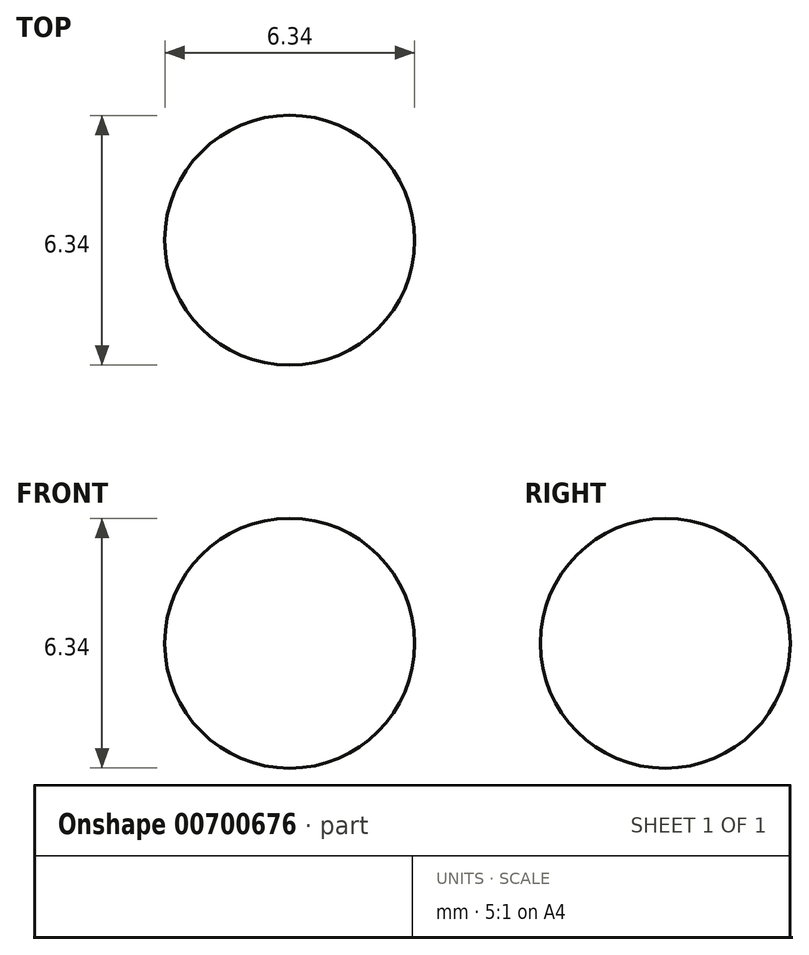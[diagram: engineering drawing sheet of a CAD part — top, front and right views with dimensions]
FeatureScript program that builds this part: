
annotation { "Feature Type Name" : "Feature", "Feature Type Description" : "" }
export const myFeature = defineFeature(function(context is Context, id is Id, definition is map)
    precondition{}
    {
        {
            var Q0;
            Q0=qCreatedBy(makeId("Front.planeOp"),FACE);
            var sketch = newSketch(context, id + "F0", { "sketchPlane" : qUnion([Q0])});
            skArc(sketch, "E0", {"start": v(0, -3.18) * mm, "mid": v(3.18, 0) * mm, "end": v(0, 3.18) * mm});
            skLineSegment(sketch, "E1", {"start": v(0, 3.18) * mm, "end": v(0, -3.18) * mm});
            skSolve(sketch);
        }
        {
            var Q0;
            Q0 = qSketchRegion(id + "F0", true);
            var Q1;
            Q1=sQuery(id+"F0.wireOp",EDGE,"E1");
            revolve(context, id + "F1", {"entities" : qUnion([Q0]), "axis" : qUnion([Q1]), "revolveType" : RevolveType.FULL});
        }
    });
